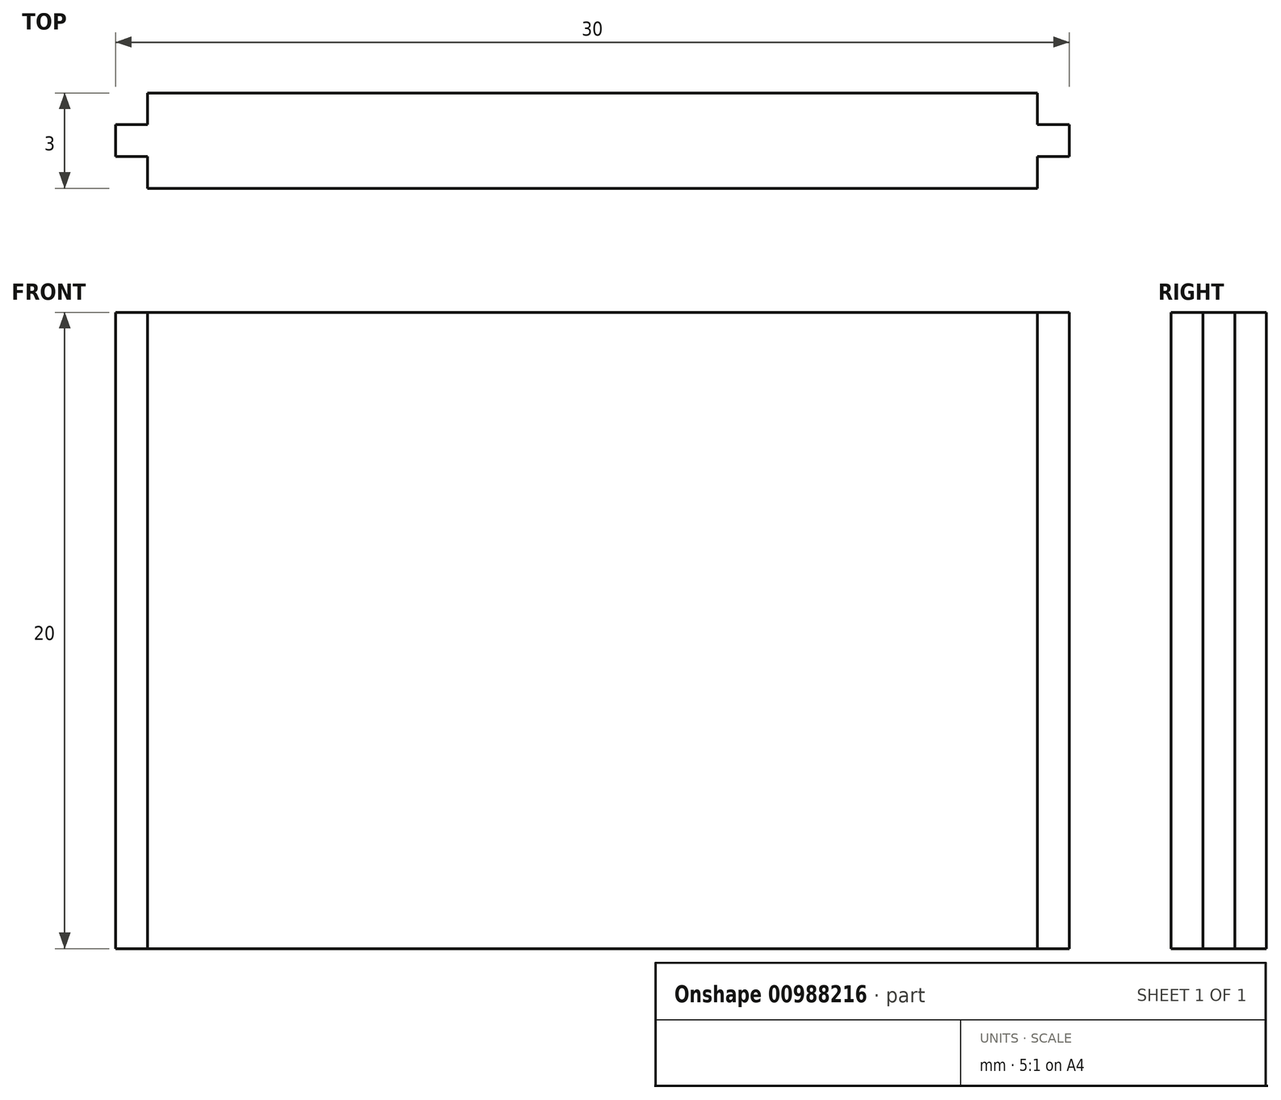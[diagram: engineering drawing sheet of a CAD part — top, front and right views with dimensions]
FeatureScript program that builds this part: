
annotation { "Feature Type Name" : "Feature", "Feature Type Description" : "" }
export const myFeature = defineFeature(function(context is Context, id is Id, definition is map)
    precondition{}
    {
        {
            var Q0;
            Q0=qCreatedBy(makeId("Top.planeOp"),FACE);
            var sketch = newSketch(context, id + "F0", { "sketchPlane" : qUnion([Q0])});
            skLineSegment(sketch, "E0.bottom", {"start": v(-14, 1.5) * mm, "end": v(14, 1.5) * mm});
            skLineSegment(sketch, "E0.top", {"start": v(-14, -1.5) * mm, "end": v(14, -1.5) * mm});
            skLineSegment(sketch, "E0.left", {"start": v(-14, 1.5) * mm, "end": v(-14, 0.5) * mm});
            skLineSegment(sketch, "E0.right", {"start": v(14, 1.5) * mm, "end": v(14, 0.5) * mm});
            skLineSegment(sketch, "E1.bottom", {"start": v(14, 0.5) * mm, "end": v(15, 0.5) * mm});
            skLineSegment(sketch, "E1.top", {"start": v(14, -0.5) * mm, "end": v(15, -0.5) * mm});
            skLineSegment(sketch, "E1.right", {"start": v(15, 0.5) * mm, "end": v(15, -0.5) * mm});
            skLineSegment(sketch, "E2.bottom", {"start": v(-14, 0.5) * mm, "end": v(-15, 0.5) * mm});
            skLineSegment(sketch, "E2.top", {"start": v(-14, -0.5) * mm, "end": v(-15, -0.5) * mm});
            skLineSegment(sketch, "E2.right", {"start": v(-15, 0.5) * mm, "end": v(-15, -0.5) * mm});
            skLineSegment(sketch, "E3.trimOffspring", {"start": v(-14, -0.5) * mm, "end": v(-14, -1.5) * mm});
            skLineSegment(sketch, "E4.trimOffspring", {"start": v(14, -0.5) * mm, "end": v(14, -1.5) * mm});
            skSolve(sketch);
        }
        {
            var Q0;
            Q0=makeQuery(id+"F0.imprint","IMPRINT",FACE,{"disambiguationData":[TD([[makeQuery(id+"F0.imprint","IMPRINT",EDGE,{"derivedFrom":sQuery(id+"F0.wireOp",EDGE,"E0.bottom")}),-1.0]])]});
            extrude(context, id + "F1", {"entities" : qUnion([Q0]), "depth" : 20 * mm, "offsetDistance" : 25 * mm});
        }
    });
